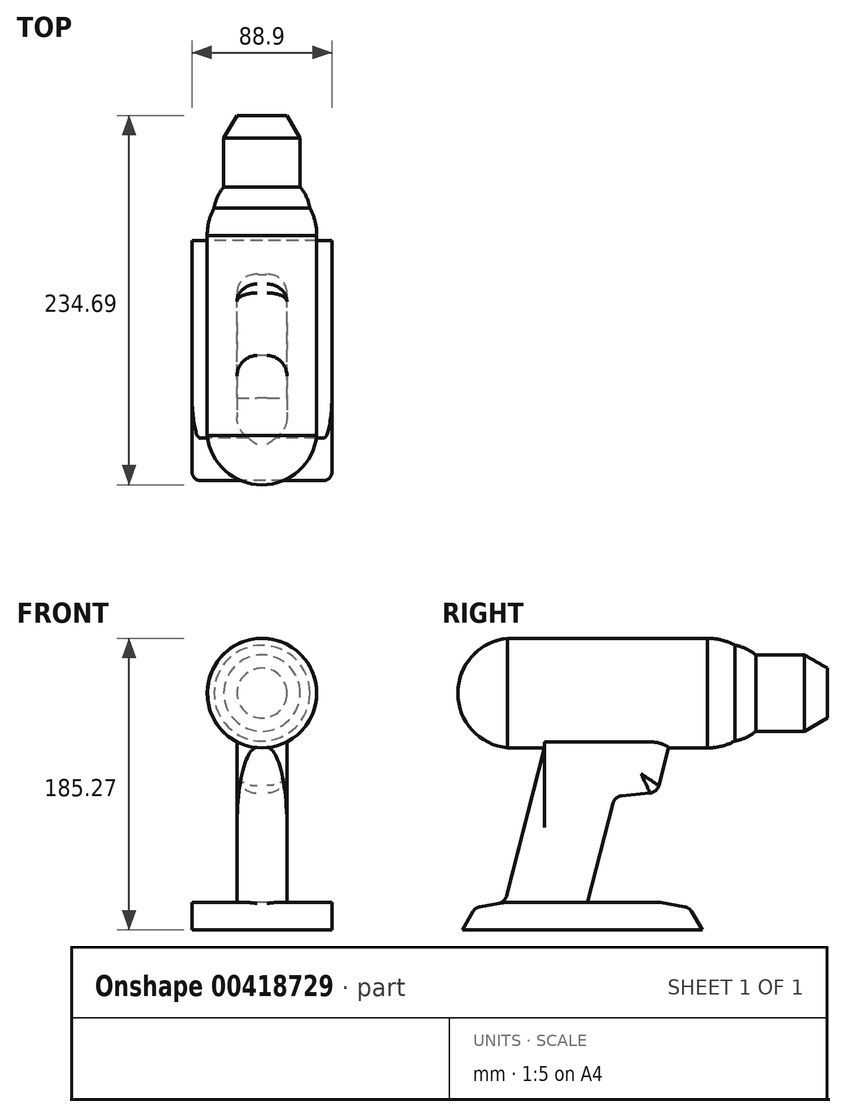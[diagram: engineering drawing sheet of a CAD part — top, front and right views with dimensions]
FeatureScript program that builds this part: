
annotation { "Feature Type Name" : "Feature", "Feature Type Description" : "" }
export const myFeature = defineFeature(function(context is Context, id is Id, definition is map)
    precondition{}
    {
        {
            var Q0;
            Q0=qCreatedBy(makeId("Right.planeOp"),FACE);
            var sketch = newSketch(context, id + "F0", { "sketchPlane" : qUnion([Q0])});
            skArc(sketch, "E0", {"start": v(-43.8, 66.68) * mm, "mid": v(-70.7, 57.8) * mm, "end": v(-82.17, 31.93) * mm});
            skLineSegment(sketch, "E1", {"start": v(-50.68, 66.68) * mm, "end": v(76.32, 66.68) * mm});
            skLineSegment(sketch, "E2", {"start": v(137.99, 56.2) * mm, "end": v(152.52, 47.8) * mm});
            skLineSegment(sketch, "E3", {"start": v(152.52, 47.8) * mm, "end": v(152.52, 31.93) * mm});
            skLineSegment(sketch, "E4.trimOffspring", {"start": v(106.99, 56.2) * mm, "end": v(137.99, 56.2) * mm});
            skArc(sketch, "E5.trimOffspring", {"start": v(93.7, 62.33) * mm, "mid": v(85.29, 65.64) * mm, "end": v(76.32, 66.68) * mm});
            skArc(sketch, "E6.trimOffspring", {"start": v(106.99, 56.2) * mm, "mid": v(100.76, 60.16) * mm, "end": v(93.7, 62.33) * mm});
            skLineSegment(sketch, "E7", {"start": v(177.55, 31.93) * mm, "end": v(-103.69, 31.93) * mm, "construction": true});
            skPoint(sketch, "E7.startSnap0", {"position": v(152.52, 31.93) * mm});
            skLineSegment(sketch, "E8", {"start": v(-82.17, 31.93) * mm, "end": v(152.52, 31.93) * mm});
            skSolve(sketch);
        }
        {
            var Q0;
            Q0=makeQuery(id+"F0.imprint","IMPRINT",FACE,{"disambiguationData":[TD([[makeQuery(id+"F0.imprint","IMPRINT",EDGE,{"derivedFrom":sQuery(id+"F0.wireOp",EDGE,"E2")}),-1.0]])]});
            var Q1;
            Q1=sQuery(id+"F0.wireOp",EDGE,"E7");
            revolve(context, id + "F1", {"entities" : qUnion([Q0]), "axis" : qUnion([Q1]), "revolveType" : RevolveType.FULL});
        }
        {
            var Q0;
            Q0=qCreatedBy(makeId("Right.planeOp"),FACE);
            var sketch = newSketch(context, id + "F2", { "sketchPlane" : qUnion([Q0])});
            skArc(sketch, "E9", {"start": v(-50.68, 66.68) * mm, "mid": v(-82.16, 32.83) * mm, "end": v(-52.47, -2.6) * mm});
            skLineSegment(sketch, "E10", {"start": v(-27.07, -2.6) * mm, "end": v(-52.47, -100.98) * mm});
            skLineSegment(sketch, "E11", {"start": v(-52.47, -100.98) * mm, "end": v(-68.24, -103.76) * mm});
            skLineSegment(sketch, "E12", {"start": v(-72.64, -106.84) * mm, "end": v(-79.42, -118.58) * mm});
            skLineSegment(sketch, "E13", {"start": v(-79.42, -118.58) * mm, "end": v(72.98, -118.58) * mm});
            skLineSegment(sketch, "E14", {"start": v(72.98, -118.58) * mm, "end": v(66.2, -106.84) * mm});
            skLineSegment(sketch, "E15", {"start": v(61.8, -103.76) * mm, "end": v(46.58, -101.08) * mm});
            skLineSegment(sketch, "E16", {"start": v(45.48, -100.98) * mm, "end": v(-52.47, -100.98) * mm});
            skLineSegment(sketch, "E17", {"start": v(0, -100.98) * mm, "end": v(16.25, -38.04) * mm});
            skLineSegment(sketch, "E18", {"start": v(21.79, -33.3) * mm, "end": v(39.84, -31.56) * mm});
            skLineSegment(sketch, "E19", {"start": v(45.38, -26.82) * mm, "end": v(51.63, -2.6) * mm});
            skLineSegment(sketch, "E20", {"start": v(-27.07, -2.6) * mm, "end": v(51.63, -2.6) * mm});
            skPoint(sketch, "E21.visualSharp", {"position": v(44.27, -31.13) * mm});
            skArc(sketch, "E21.filletArc", {"start": v(39.84, -31.56) * mm, "mid": v(43.36, -30.06) * mm, "end": v(45.38, -26.82) * mm});
            skPoint(sketch, "E22.visualSharp", {"position": v(17.36, -33.73) * mm});
            skArc(sketch, "E22.filletArc", {"start": v(21.79, -33.3) * mm, "mid": v(18.27, -34.8) * mm, "end": v(16.25, -38.04) * mm});
            skPoint(sketch, "E23.visualSharp", {"position": v(0, -100.98) * mm});
            skPoint(sketch, "E24.visualSharp", {"position": v(46.03, -100.98) * mm});
            skArc(sketch, "E24.filletArc", {"start": v(46.58, -101.08) * mm, "mid": v(46.03, -101) * mm, "end": v(45.48, -100.98) * mm});
            skPoint(sketch, "E25.visualSharp", {"position": v(64.72, -104.27) * mm});
            skArc(sketch, "E25.filletArc", {"start": v(66.2, -106.84) * mm, "mid": v(64.35, -104.81) * mm, "end": v(61.8, -103.76) * mm});
            skPoint(sketch, "E26.visualSharp", {"position": v(-71.16, -104.27) * mm});
            skArc(sketch, "E26.filletArc", {"start": v(-68.24, -103.76) * mm, "mid": v(-70.78, -104.81) * mm, "end": v(-72.64, -106.84) * mm});
            skPoint(sketch, "E27.visualSharp", {"position": v(-52.47, -100.98) * mm});
            skSolve(sketch);
        }
        {
            var Q0;
            {var subQ2=sQuery(id+"F2.wireOp",EDGE,"E10");Q0=makeQuery(id+"F2.imprint","IMPRINT",FACE,{"disambiguationData":[TD([[makeQuery(id+"F2.imprint","IMPRINT",EDGE,{"derivedFrom":subQ2}),1.0]])]});}
            extrude(context, id + "F3", {"entities" : qUnion([Q0]), "operationType" : NewBodyOperationType.ADD, "endBound" : BoundingType.SYMMETRIC, "depth" : 31.75 * mm});
        }
        {
            var Q0;
            {var subQ0=sQuery(id+"F2.wireOp",EDGE,"E10");var subQ1=sQuery(id+"F2.wireOp",EDGE,"E20");var subQ2=sQuery(id+"F2.wireOp",EDGE,"E19");Q0=makeQuery(id+"F3.boolean.opBoolean","SPLIT",FACE,{"disambiguationData":[TD([makeQuery(id+"F3.opExtrude","CAP_FACE",FACE,{"disambiguationData":[OSD([subQ0,sQuery(id+"F2.wireOp",EDGE,"E16"),sQuery(id+"F2.wireOp",EDGE,"E17"),sQuery(id+"F2.wireOp",EDGE,"E18"),subQ2,subQ1,sQuery(id+"F2.wireOp",EDGE,"E21.filletArc"),sQuery(id+"F2.wireOp",EDGE,"E22.filletArc")])],"isStart":false})])],"derivedFrom":makeQuery(id+"F3.opExtrude","SWEPT_FACE",FACE,{"disambiguationData":[OSD([subQ1])]})});}
            var Q1;
            {var subQ0=sQuery(id+"F2.wireOp",EDGE,"E10");var subQ1=sQuery(id+"F2.wireOp",EDGE,"E20");var subQ2=sQuery(id+"F2.wireOp",EDGE,"E19");Q1=makeQuery(id+"F3.boolean.opBoolean","SPLIT",FACE,{"disambiguationData":[TD([makeQuery(id+"F3.opExtrude","CAP_FACE",FACE,{"disambiguationData":[OSD([subQ0,sQuery(id+"F2.wireOp",EDGE,"E16"),sQuery(id+"F2.wireOp",EDGE,"E17"),sQuery(id+"F2.wireOp",EDGE,"E18"),subQ2,subQ1,sQuery(id+"F2.wireOp",EDGE,"E21.filletArc"),sQuery(id+"F2.wireOp",EDGE,"E22.filletArc")])],"isStart":true})])],"derivedFrom":makeQuery(id+"F3.opExtrude","SWEPT_FACE",FACE,{"disambiguationData":[OSD([subQ1])]})});}
            var Q2;
            Q2=makeQuery(id+"F1.opRevolve","SWEPT_FACE",FACE,{"disambiguationData":[OSD([sQuery(id+"F0.wireOp",EDGE,"E1")])]});
            extrude(context, id + "F4", {"entities" : qUnion([Q0, Q1]), "operationType" : NewBodyOperationType.ADD, "endBound" : BoundingType.UP_TO_SURFACE, "endBoundEntityFace" : qUnion([Q2]), "depth" : 25.4 * mm});
        }
        {
            var Q0;
            {var subQ1=sQuery(id+"F2.wireOp",EDGE,"E11");Q0=makeQuery(id+"F2.imprint","IMPRINT",FACE,{"disambiguationData":[TD([[makeQuery(id+"F2.imprint","IMPRINT",EDGE,{"derivedFrom":subQ1}),1.0]])]});}
            extrude(context, id + "F5", {"entities" : qUnion([Q0]), "operationType" : NewBodyOperationType.ADD, "endBound" : BoundingType.SYMMETRIC, "depth" : 88.9 * mm});
        }
        {
            var Q0;
            {var subQ0=sQuery(id+"F2.wireOp",EDGE,"E20");Q0=makeQuery(id+"F4.opExtrude","CAP_EDGE",EDGE,{"disambiguationData":[OSD([subQ0]),TDD([makeQuery(id+"F3.opExtrude","CAP_EDGE",EDGE,{"disambiguationData":[OSD([subQ0])],"isStart":false})])],"isStart":false});}
            var Q1;
            {var subQ0=sQuery(id+"F2.wireOp",EDGE,"E20");Q1=makeQuery(id+"F4.opExtrude","CAP_EDGE",EDGE,{"disambiguationData":[OSD([subQ0]),TDD([makeQuery(id+"F3.opExtrude","CAP_EDGE",EDGE,{"disambiguationData":[OSD([subQ0])],"isStart":true})])],"isStart":false});}
            var Q2;
            Q2=makeQuery(id+"F3.opExtrude","CAP_EDGE",EDGE,{"disambiguationData":[OSD([sQuery(id+"F2.wireOp",EDGE,"E16")])],"isStart":false});
            var Q3;
            Q3=makeQuery(id+"F3.opExtrude","CAP_EDGE",EDGE,{"disambiguationData":[OSD([sQuery(id+"F2.wireOp",EDGE,"E16")])],"isStart":true});
            var Q4;
            Q4=makeQuery(id+"F3.opExtrude","SWEPT_EDGE",EDGE,{"disambiguationData":[OSD([sQuery(id+"F2.wireOp",EDGE,"E16"),sQuery(id+"F2.wireOp",EDGE,"E17")])]});
            var Q5;
            {var subQ0=sQuery(id+"F2.wireOp",EDGE,"E16");var subQ1=sQuery(id+"F2.wireOp",EDGE,"E11");var subQ2=sQuery(id+"F2.wireOp",EDGE,"E10");Q5=makeQuery(id+"F5.boolean.opBoolean","MERGE",EDGE,{"derivedFrom":[makeQuery(id+"F3.opExtrude","SWEPT_EDGE",EDGE,{"disambiguationData":[OSD([subQ2,subQ1,subQ0])]}),makeQuery(id+"F5.opExtrude","SWEPT_EDGE",EDGE,{"disambiguationData":[OSD([subQ2,subQ1,subQ0])]})]});}
            fillet(context, id + "F6", {"entities" : qUnion([Q0, Q1, Q2, Q3, Q4, Q5]), "radius" : 6.35 * mm, "tangentPropagation" : true, "allowEdgeOverflow" : false});
        }
        {
            var Q0;
            Q0=makeQuery(id+"F3.opExtrude","CAP_EDGE",EDGE,{"disambiguationData":[OSD([sQuery(id+"F2.wireOp",EDGE,"E10")])],"isStart":false});
            var Q1;
            Q1=makeQuery(id+"F3.opExtrude","CAP_EDGE",EDGE,{"disambiguationData":[OSD([sQuery(id+"F2.wireOp",EDGE,"E10")])],"isStart":true});
            var Q2;
            Q2=makeQuery(id+"F3.opExtrude","CAP_EDGE",EDGE,{"disambiguationData":[OSD([sQuery(id+"F2.wireOp",EDGE,"E17")])],"isStart":false});
            var Q3;
            Q3=makeQuery(id+"F3.opExtrude","CAP_EDGE",EDGE,{"disambiguationData":[OSD([sQuery(id+"F2.wireOp",EDGE,"E17")])],"isStart":true});
            fillet(context, id + "F7", {"entities" : qUnion([Q0, Q1, Q2, Q3]), "radius" : 12.7 * mm, "tangentPropagation" : true, "allowEdgeOverflow" : false});
        }
        {
            var Q0;
            Q0=makeQuery(id+"F5.opExtrude","CAP_EDGE",EDGE,{"disambiguationData":[OSD([sQuery(id+"F2.wireOp",EDGE,"E12")])],"isStart":false});
            var Q1;
            Q1=makeQuery(id+"F5.opExtrude","CAP_EDGE",EDGE,{"disambiguationData":[OSD([sQuery(id+"F2.wireOp",EDGE,"E12")])],"isStart":true});
            fillet(context, id + "F8", {"entities" : qUnion([Q0, Q1]), "radius" : 5.08 * mm, "tangentPropagation" : true, "allowEdgeOverflow" : false});
        }
    });
